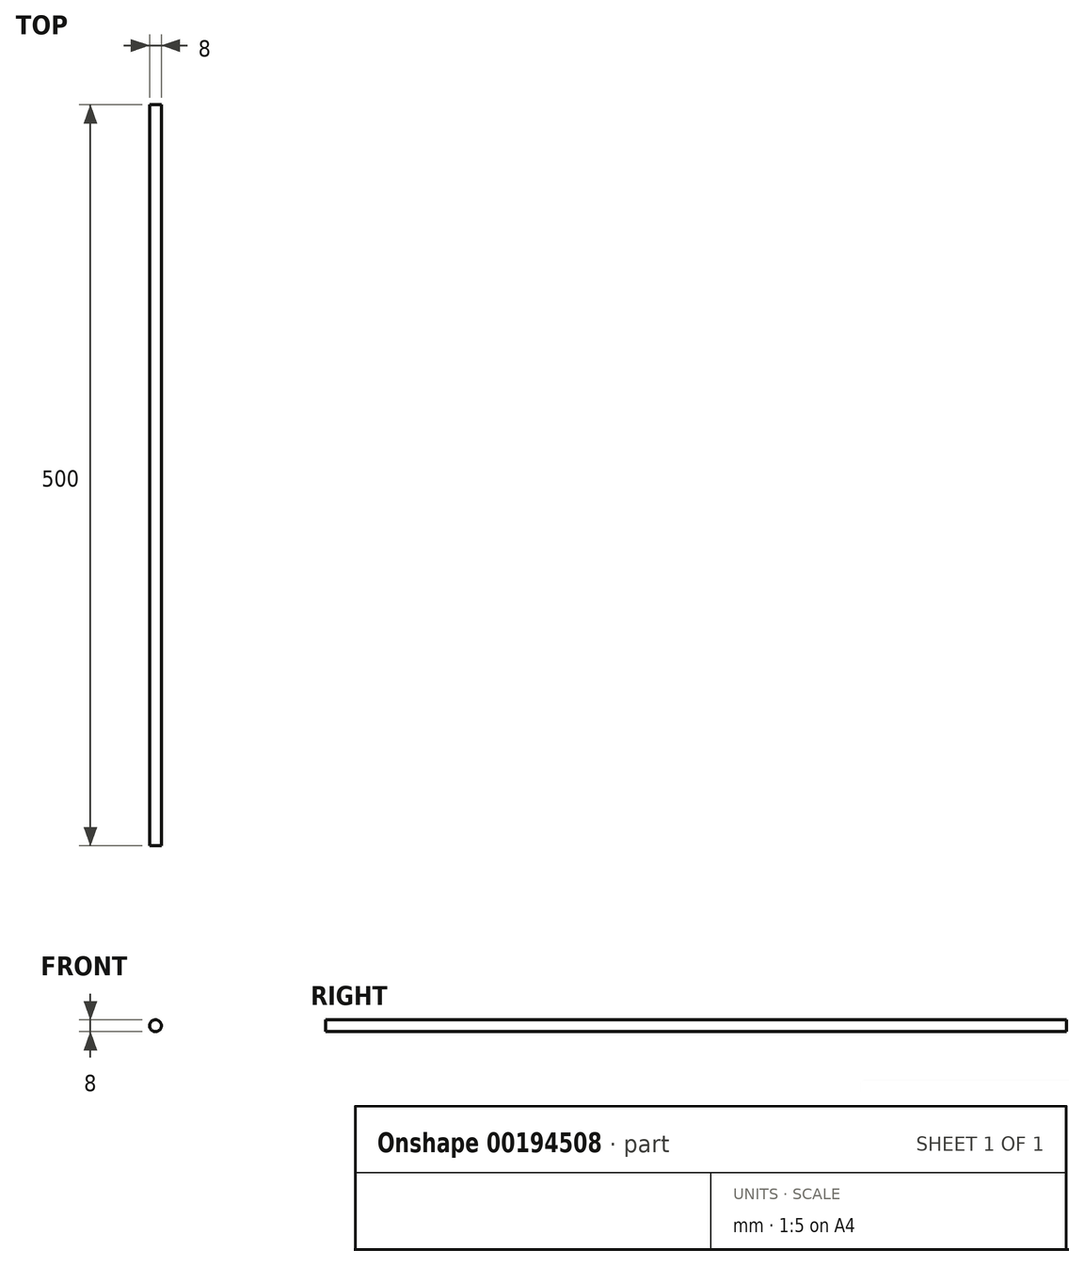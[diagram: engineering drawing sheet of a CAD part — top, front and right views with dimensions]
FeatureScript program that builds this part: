
annotation { "Feature Type Name" : "Feature", "Feature Type Description" : "" }
export const myFeature = defineFeature(function(context is Context, id is Id, definition is map)
    precondition{}
    {
        {
            var Q0;
            Q0=qCreatedBy(makeId("Front.planeOp"),FACE);
            var sketch = newSketch(context, id + "F0", { "sketchPlane" : qUnion([Q0])});
            skCircle(sketch, "E0", {"center": v(0, 0) * mm, "radius": 4 * mm});
            skSolve(sketch);
        }
        {
            var Q0;
            Q0 = qSketchRegion(id + "F0", true);
            var Q1;
            Q1=makeQuery(id+"F0.imprint","IMPRINT",FACE,{"disambiguationData":[TD([[makeQuery(id+"F0.imprint","IMPRINT",EDGE,{"derivedFrom":sQuery(id+"F0.wireOp",EDGE,"E0")}),1.0]])]});
            extrude(context, id + "F1", {"entities" : qUnion([Q0, Q1]), "depth" : 500 * mm});
        }
    });
